# Revit family: Camera-Security-Panasonic-Super_Dynamic-Vandal_Resistant-Waterproof--H265_Varifocal-Dome-Network-U2532LSeriesX
name_source: partatom
category: Security Devices
revit_build: Autodesk Revit 2016 (Build: 20190507_1515(x64)
units: mm (PartAtom-declared; Revit-internal decimal feet)

## family parameters
Cut with Voids When Loaded = No
Host = Face
Maintain Annotation Orientation = No
OmniClass Number = 23.85.10.14.11
OmniClass Title = Cameras
Part Type = Normal
Room Calculation Point = No
Round Connector Dimension = Use Diameter
Shared = No

## types (2) — shared parameters
Angle Of View = 100
Communication Ports = 10Base-T / 100Base-TX, RJ45 connector
Date Last Modified = 2020/01/28
Day Or Night = Yes
Diameter = 154 mm  [stored 0.505249 ft]
Equipment Abbreviation = SC
Family Version = 1.0.0
HFOV Max 169 = 100.00°
HFOV Min 169 = 43.00°
Has POE = Yes
Height = 103 mm  [stored 0.337927 ft]
IP Or Analog = IP
Indoor Or Outdoor = Outdoor
Manufacturer = Panasonic
Model Disclaimer = Contact Panasonic for more information
Mounting Positions = Mount Dependent or Surface Mount
Operational Humidity = 10 to 100 % (no condensation)
Operational Temperature = -30 °C to +50 °C (-22 °F to +122 °F)
Pan Max = 285.00°
Pan Min = -75.00°
Panning Range = -75 to +285
Product Documentation Link = https://bizpartner.panasonic.net
Product Material = Paint - Panasonic - i-PRO White
Product Page URL = https://security.panasonic.com
Provide Feedback = https://www.surveymonkey.com
Regulatory Compliance = UL (UL60950-1), c-UL (CSA C22.2 No.60950-1), CE, IEC60950-1, FCC (Part15 ClassA), ICES003 ClassA, EN55032 ClassB, EN55024
Shock Resistance = IK10 (IEC 62262)
Storage Temperature = -30 °C to +50 °C (-22 °F to +122 °F)
Tilt Max = 85.00°
Tilt Min = -30.00°
Tilting Range = -30 to +85
URL = http://security.panasonic.com
VFOV Min 169 = 24.00°
Vandal Resistant = Yes
Voltage DC = 48 V
Water and Dust Resistance = IP66 (IEC 60529), Type 4X (UL50E), NEMA 4X compliant
Wide Dynamic Range = Yes
Yaw Max = 100.00°
Yaw Min = -100.00°
Yawing Range = -100 to +100
z Base Height = 55.7 mm  [stored 0.182743 ft]
z Base Radius = 77 mm  [stored 0.252625 ft]
z Ceiling Mount Bottom Offset = -42.5 mm  [stored -0.139436 ft]
z Const Pan Handle Length = 495 mm  [stored 1.62402 ft]
z Const Tilt Base Length = 250 mm  [stored 0.82021 ft]
z Const Tilt Base2 Length = 500 mm  [stored 1.64042 ft]
z Const Tilt Handle Length = 300 mm
z Const Yaw Base Length = 260 mm  [stored 0.853018 ft]
z Const Yaw Base2 Length = 440 mm  [stored 1.44357 ft]
z Const Yaw Handle Length = 235 mm  [stored 0.770997 ft]
z Dome Radius = 47.3 mm  [stored 0.155184 ft]
z Half Height of LowerBase = 21.5 mm  [stored 0.0705381 ft]
z Has Ceiling Mount Bracket = No
z Has Wall Mount Bracket = No
z Level Offset = 500 mm  [stored 1.64042 ft]
z VV Origin HeightX = 61.5 mm  [stored 0.201772 ft]
z VV Viewpoint Depth Max = 32.6 mm
z VV Viewpoint Depth Min = 32.6 mm
zero-valued in all types: Default Elevation, z Zero

## per-type parameters (varying)
| type | Camera Type | Description | HFOV Max 43 | HFOV Min 43 | Minimum Illumination | Part Description | Power Active | VFOV Max 169 | VFOV Max 43 | VFOV Min 43 |
| WV-U2532L | 2532 | Security Camera, Fixed Dome, Network, Super Dynamic Vandal Resistant  Weatherproof, H.265 Varifocal, FullHD | 82.00° | 35.00° | 0.100 lx | Security Camera, Fixed Dome, Network, Super Dynamic Vandal Resistant  Weatherproof, H.265 Varifocal, FullHD | 6.7 W | 55.00° | 61.00° | 27.00° |
| WV-U2542L | 2542 | Security Camera, Fixed Dome, Network, Super Dynamic Vandal Resistant  Weatherproof, H.265 Varifocal, WQHD | 100.00° | 43.00° | 0.300 lx | Security Camera, Fixed Dome, Network, Super Dynamic Vandal Resistant  Weatherproof, H.265 Varifocal, WQHD | 7.2 W | 56.00° | 56.00° | 24.00° |

note: column(s) folded — value = type name in every type: Model, Part Number

note: [stored X ft] marks values corroborated as IEEE doubles in the binary element streams (Revit-internal decimal feet)

## geometry (parser evidence)
native form markers: Blend x2, Sweep x7
no freeform markers — native parametric forms only
